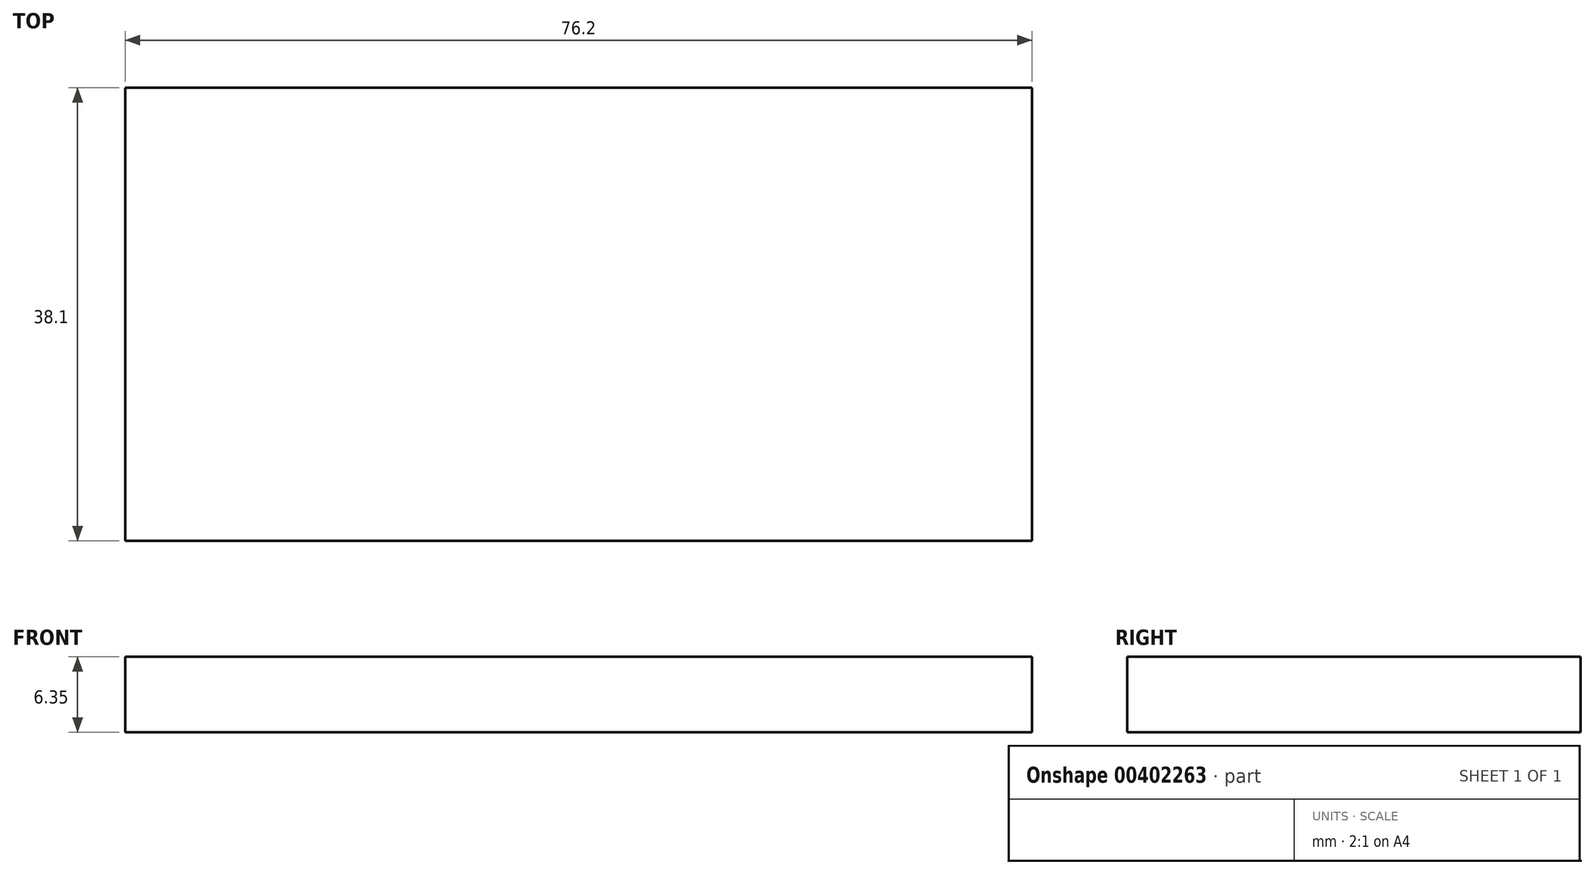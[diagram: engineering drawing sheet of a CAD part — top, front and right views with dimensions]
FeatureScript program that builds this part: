
annotation { "Feature Type Name" : "Feature", "Feature Type Description" : "" }
export const myFeature = defineFeature(function(context is Context, id is Id, definition is map)
    precondition{}
    {
        {
            var Q0;
            Q0=qCreatedBy(makeId("Top.planeOp"),FACE);
            var sketch = newSketch(context, id + "F0", { "sketchPlane" : qUnion([Q0])});
            skLineSegment(sketch, "E0.bottom", {"start": v(38.1, 19.05) * mm, "end": v(-38.1, 19.05) * mm});
            skLineSegment(sketch, "E0.top", {"start": v(38.1, -19.05) * mm, "end": v(-38.1, -19.05) * mm});
            skLineSegment(sketch, "E0.left", {"start": v(38.1, 19.05) * mm, "end": v(38.1, -19.05) * mm});
            skLineSegment(sketch, "E0.right", {"start": v(-38.1, 19.05) * mm, "end": v(-38.1, -19.05) * mm});
            skPoint(sketch, "E0.middle", {"position": v(0, 0) * mm});
            skSolve(sketch);
        }
        {
            var Q0;
            Q0=makeQuery(id+"F0.imprint","IMPRINT",FACE,{"disambiguationData":[TD([[makeQuery(id+"F0.imprint","IMPRINT",EDGE,{"derivedFrom":sQuery(id+"F0.wireOp",EDGE,"E0.bottom")}),1.0]])]});
            extrude(context, id + "F1", {"entities" : qUnion([Q0]), "oppositeDirection" : true, "depth" : 6.35 * mm});
        }
    });
